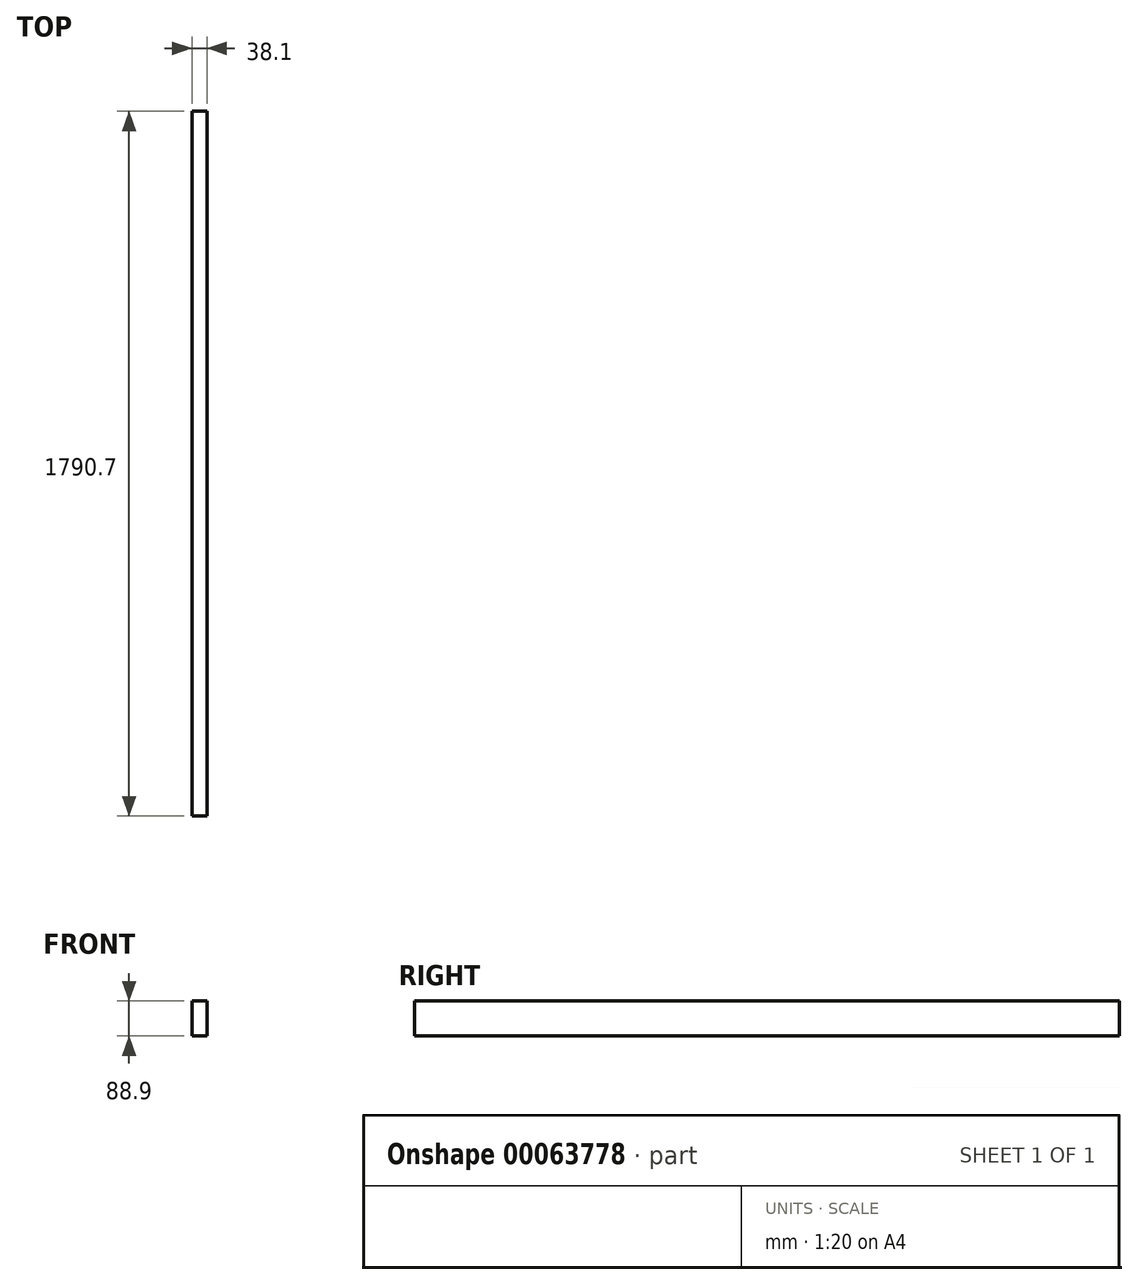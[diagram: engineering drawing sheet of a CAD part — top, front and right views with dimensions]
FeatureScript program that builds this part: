
annotation { "Feature Type Name" : "Feature", "Feature Type Description" : "" }
export const myFeature = defineFeature(function(context is Context, id is Id, definition is map)
    precondition{}
    {
        {
            var Q0;
            Q0=qCreatedBy(makeId("Front.planeOp"),FACE);
            var sketch = newSketch(context, id + "F0", { "sketchPlane" : qUnion([Q0])});
            skLineSegment(sketch, "E0.bottom", {"start": v(-18, 55.77) * mm, "end": v(20.1, 55.77) * mm});
            skLineSegment(sketch, "E0.top", {"start": v(-18, -33.13) * mm, "end": v(20.1, -33.13) * mm});
            skLineSegment(sketch, "E0.left", {"start": v(-18, 55.77) * mm, "end": v(-18, -33.13) * mm});
            skLineSegment(sketch, "E0.right", {"start": v(20.1, 55.77) * mm, "end": v(20.1, -33.13) * mm});
            skSolve(sketch);
        }
        {
            var Q0;
            Q0=qSketchRegion(id+"F0",true);
            extrude(context, id + "F1", {"entities" : qUnion([Q0]), "endBound" : BoundingType.SYMMETRIC, "depth" : 1790.7 * mm});
        }
    });
